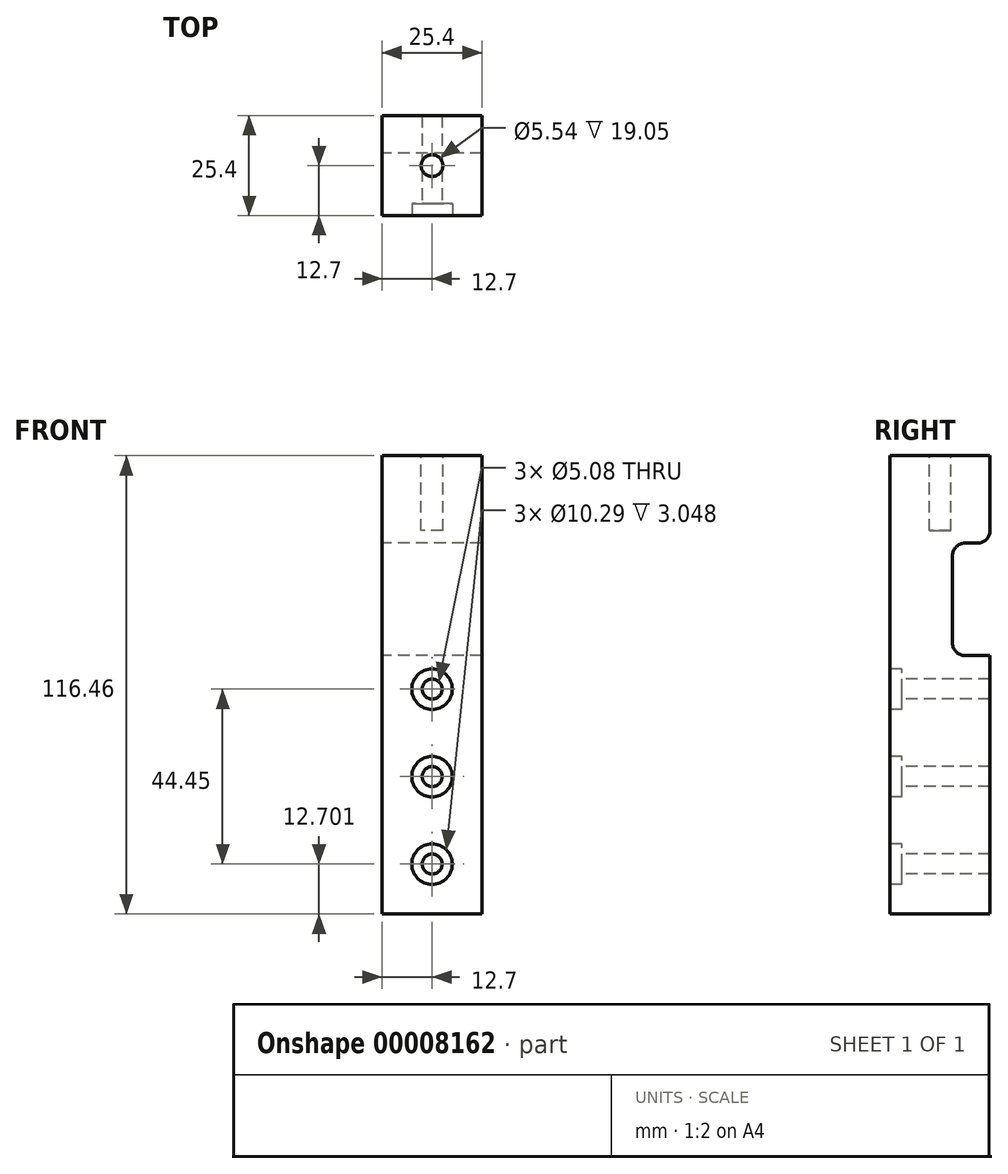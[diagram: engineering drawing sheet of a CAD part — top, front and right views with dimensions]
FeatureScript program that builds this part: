
annotation { "Feature Type Name" : "Feature", "Feature Type Description" : "" }
export const myFeature = defineFeature(function(context is Context, id is Id, definition is map)
    precondition{}
    {
        {
            var Q0;
            Q0=qCreatedBy(makeId("Top.planeOp"),FACE);
            var sketch = newSketch(context, id + "F0", { "sketchPlane" : qUnion([Q0])});
            skLineSegment(sketch, "E0", {"start": v(25.4, -25.4) * mm, "end": v(0, -25.4) * mm});
            skLineSegment(sketch, "E1", {"start": v(25.4, -25.4) * mm, "end": v(25.4, 0) * mm});
            skLineSegment(sketch, "E2", {"start": v(25.4, 0) * mm, "end": v(0, 0) * mm});
            skLineSegment(sketch, "E3", {"start": v(0, 0) * mm, "end": v(0, -25.4) * mm});
            skSolve(sketch);
        }
        {
            var Q0;
            Q0 = qSketchRegion(id + "F0", true);
            extrude(context, id + "F1", {"entities" : qUnion([Q0]), "oppositeDirection" : true, "depth" : 116.46 * mm});
        }
        {
            var Q0;
            Q0=makeQuery(id+"F1.opExtrude","SWEPT_FACE",FACE,{"disambiguationData":[OSD([sQuery(id+"F0.wireOp",EDGE,"E0")])]});
            var sketch = newSketch(context, id + "F2", { "sketchPlane" : qUnion([Q0])});
            skLineSegment(sketch, "E4", {"start": v(12.7, 0) * mm, "end": v(12.7, -116.46) * mm, "construction": true});
            skCircle(sketch, "E5", {"center": v(12.7, -103.76) * mm, "radius": 2.54 * mm});
            skCircle(sketch, "E6", {"center": v(12.7, -59.3) * mm, "radius": 2.54 * mm});
            skCircle(sketch, "E7", {"center": v(12.7, -81.53) * mm, "radius": 2.54 * mm});
            skSolve(sketch);
        }
        {
            var Q0;
            Q0 = qSketchRegion(id + "F2", true);
            var Q1;
            Q1=makeQuery(id+"F1.opExtrude","SWEPT_FACE",FACE,{"disambiguationData":[OSD([sQuery(id+"F0.wireOp",EDGE,"E2")])]});
            extrude(context, id + "F3", {"entities" : qUnion([Q0]), "operationType" : NewBodyOperationType.REMOVE, "endBound" : BoundingType.UP_TO_SURFACE, "oppositeDirection" : true, "endBoundEntityFace" : qUnion([Q1]), "depth" : 25.4 * mm});
        }
        {
            var Q0;
            Q0=makeQuery(id+"F1.opExtrude","SWEPT_FACE",FACE,{"disambiguationData":[OSD([sQuery(id+"F0.wireOp",EDGE,"E0")])]});
            var sketch = newSketch(context, id + "F4", { "sketchPlane" : qUnion([Q0])});
            skCircle(sketch, "E8", {"center": v(12.7, -59.3) * mm, "radius": 5.14 * mm});
            skCircle(sketch, "E9", {"center": v(12.7, -103.76) * mm, "radius": 5.14 * mm});
            skCircle(sketch, "E10", {"center": v(12.7, -81.53) * mm, "radius": 5.14 * mm});
            skSolve(sketch);
        }
        {
            var Q0;
            Q0 = qSketchRegion(id + "F4", true);
            var Q1;
            Q1=makeQuery(id+"F1.opExtrude","SWEPT_FACE",FACE,{"disambiguationData":[OSD([sQuery(id+"F0.wireOp",EDGE,"dac9d5d1-86b3-4191-af69-7b731b96aa90.right")])]});
            extrude(context, id + "F5", {"entities" : qUnion([Q0]), "operationType" : NewBodyOperationType.REMOVE, "oppositeDirection" : true, "endBoundEntity" : qUnion([Q1]), "depth" : 3.05 * mm});
        }
        {
            var Q0;
            Q0=makeQuery(id+"F1.opExtrude","CAP_FACE",FACE,{"disambiguationData":[OSD([sQuery(id+"F0.wireOp",EDGE,"E0"),sQuery(id+"F0.wireOp",EDGE,"E1"),sQuery(id+"F0.wireOp",EDGE,"E2"),sQuery(id+"F0.wireOp",EDGE,"E3")])],"isStart":true});
            var sketch = newSketch(context, id + "F6", { "sketchPlane" : qUnion([Q0])});
            skCircle(sketch, "E11", {"center": v(12.7, -12.7) * mm, "radius": 2.77 * mm});
            skSolve(sketch);
        }
        {
            var Q0;
            Q0 = qSketchRegion(id + "F6", true);
            extrude(context, id + "F7", {"entities" : qUnion([Q0]), "operationType" : NewBodyOperationType.REMOVE, "oppositeDirection" : true, "depth" : 19.05 * mm});
        }
        {
            var Q0;
            Q0=makeQuery(id+"F1.opExtrude","SWEPT_FACE",FACE,{"disambiguationData":[OSD([sQuery(id+"F0.wireOp",EDGE,"E2")])]});
            var sketch = newSketch(context, id + "F8", { "sketchPlane" : qUnion([Q0])});
            skLineSegment(sketch, "E12.bottom", {"start": v(-25.4, -22.23) * mm, "end": v(0, -22.23) * mm});
            skLineSegment(sketch, "E12.top", {"start": v(-25.4, -50.8) * mm, "end": v(0, -50.8) * mm});
            skLineSegment(sketch, "E12.left", {"start": v(-25.4, -22.23) * mm, "end": v(-25.4, -50.8) * mm});
            skLineSegment(sketch, "E12.right", {"start": v(0, -22.23) * mm, "end": v(0, -50.8) * mm});
            skSolve(sketch);
        }
        {
            var Q0;
            Q0 = qSketchRegion(id + "F8", true);
            extrude(context, id + "F9", {"entities" : qUnion([Q0]), "operationType" : NewBodyOperationType.REMOVE, "oppositeDirection" : true, "depth" : 9.52 * mm});
        }
        {
            var Q0;
            Q0=makeQuery(id+"F9.boolean.opBoolean","COPY",EDGE,{"derivedFrom":makeQuery(id+"F9.opExtrude","CAP_EDGE",EDGE,{"disambiguationData":[OSD([sQuery(id+"F8.wireOp",EDGE,"E12.bottom")])],"isStart":true})});
            var Q1;
            Q1=makeQuery(id+"F9.boolean.opBoolean","COPY",EDGE,{"derivedFrom":makeQuery(id+"F9.opExtrude","CAP_EDGE",EDGE,{"disambiguationData":[OSD([sQuery(id+"F8.wireOp",EDGE,"E12.bottom")])],"isStart":false})});
            var Q2;
            Q2=makeQuery(id+"F9.boolean.opBoolean","COPY",EDGE,{"derivedFrom":makeQuery(id+"F9.opExtrude","CAP_EDGE",EDGE,{"disambiguationData":[OSD([sQuery(id+"F8.wireOp",EDGE,"E12.top")])],"isStart":false})});
            var Q3;
            Q3=makeQuery(id+"F9.boolean.opBoolean","COPY",EDGE,{"derivedFrom":makeQuery(id+"F9.opExtrude","CAP_EDGE",EDGE,{"disambiguationData":[OSD([sQuery(id+"F8.wireOp",EDGE,"E12.top")])],"isStart":true})});
            fillet(context, id + "F10", {"entities" : qUnion([Q0, Q1, Q2, Q3]), "radius" : 3.17 * mm, "allowEdgeOverflow" : false});
        }
    });
